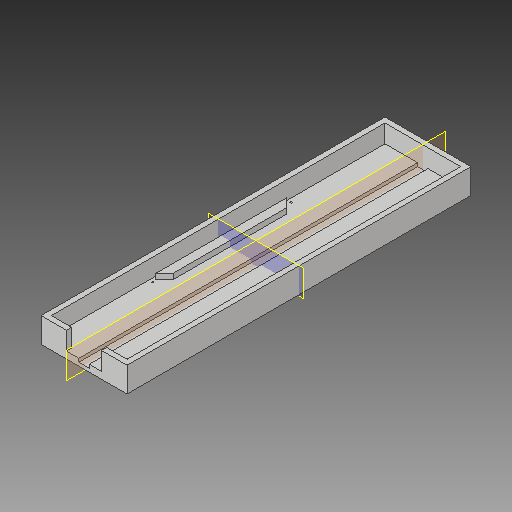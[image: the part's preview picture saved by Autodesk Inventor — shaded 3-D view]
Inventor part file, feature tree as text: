
AUTODESK INVENTOR PART (.ipt)
format: ipt  version: 2017 (Build 210142000, 142)  size: 171,008 bytes
history: native  units: mm
features: sketch x5, extrude x4, draft x4, plane x2, hole x1
ambient origin geometry x8: Origin, YZ Plane, XZ Plane, XY Plane, X Axis, Y Axis, Z Axis, Center Point
bodies: Solid1 (feature_tree)
feature tree (16):
  extrude  "Base"  Depth=200.0mm
  extrude  "Muros"  Depth=3.0mm
  extrude  "Rail"  Depth=10.5mm TaperAngle=0.0deg
  extrude  "Extrusion4"  Depth=2.0mm
  draft  "FaceDraft1"
  draft  "FaceDraft2"
  draft  "FaceDraft3"
  draft  "FaceDraft4"
  plane  "Work Plane1"
  plane  "Work Plane2"
  hole  "Hole1"  [1 undecoded]
  sketch  "Sketch1"  dims[d1=50.0mm d2=200.0mm]
  sketch  "Sketch3"  dims[d4=4.0mm d3=0.0mm d10=3.0mm]
  sketch  "Sketch4"  dims[d11=20.4mm d12=10.5mm d13=0.0mm]
  sketch  "Sketch5"  dims[d14=6.0mm d15=2.0mm]
  sketch  "Sketch6"  dims[d16=0.0mm d17=30.4mm d18=62.0mm d19=76.0mm d20=5.0mm d21=3.2mm d22=0.0mm d23=45.0deg d24=45.0deg d25=45.0deg d26=45.0deg d27=2.2mm d28=2.2mm d29=2.2mm d30=2.2mm d31=1.0mm d32=6.0mm d33=4.0mm d34=2.0mm d35=90.0deg d36=8.0mm d37=20.594885mm]
note: 1 required parameter value undecoded (feature->parameter linkage not recoverable at this tier; creation-order binding heuristic only, values carry confidence <= 0.55)
